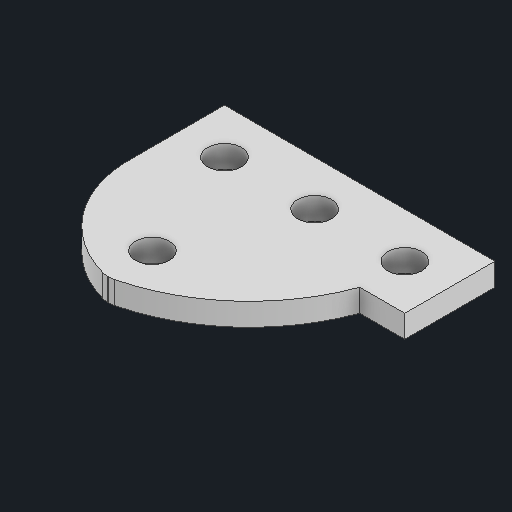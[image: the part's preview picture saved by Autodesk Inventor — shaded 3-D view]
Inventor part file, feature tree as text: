
AUTODESK INVENTOR PART (.ipt)
format: ipt  version: 2024 (Build 280153000, 153)  size: 216,064 bytes
history: native  units: in
note: dims shown in document units (in); Inventor stores cm internally (conversion verified against a paired STEP export)
features: sketch x1, extrude x1, hole x1
ambient origin geometry x8: Origin, YZ Plane, XZ Plane, XY Plane, X Axis, Y Axis, Z Axis, Center Point
bodies: Solid1 (feature_tree)
feature tree (3):
  sketch  "Sketch1"  dims[d0=1.5in d1=0.5in d2=0.5in d3=0.5in d4=0.4in d6=0.5in d7=0.25in d8=0.125in d9=0.0in d13=0.1875in d14=0.75in d15=0.375in d16=0.25in d17=0.5635in d18=1.0in d19=0.8108in d20=0.125in]
  extrude  "Extrusion1"  Depth=0.5in
  hole  "Hole1"  [1 undecoded]
note: 1 required parameter value undecoded (feature->parameter linkage not recoverable at this tier; creation-order binding heuristic only, values carry confidence <= 0.55)
